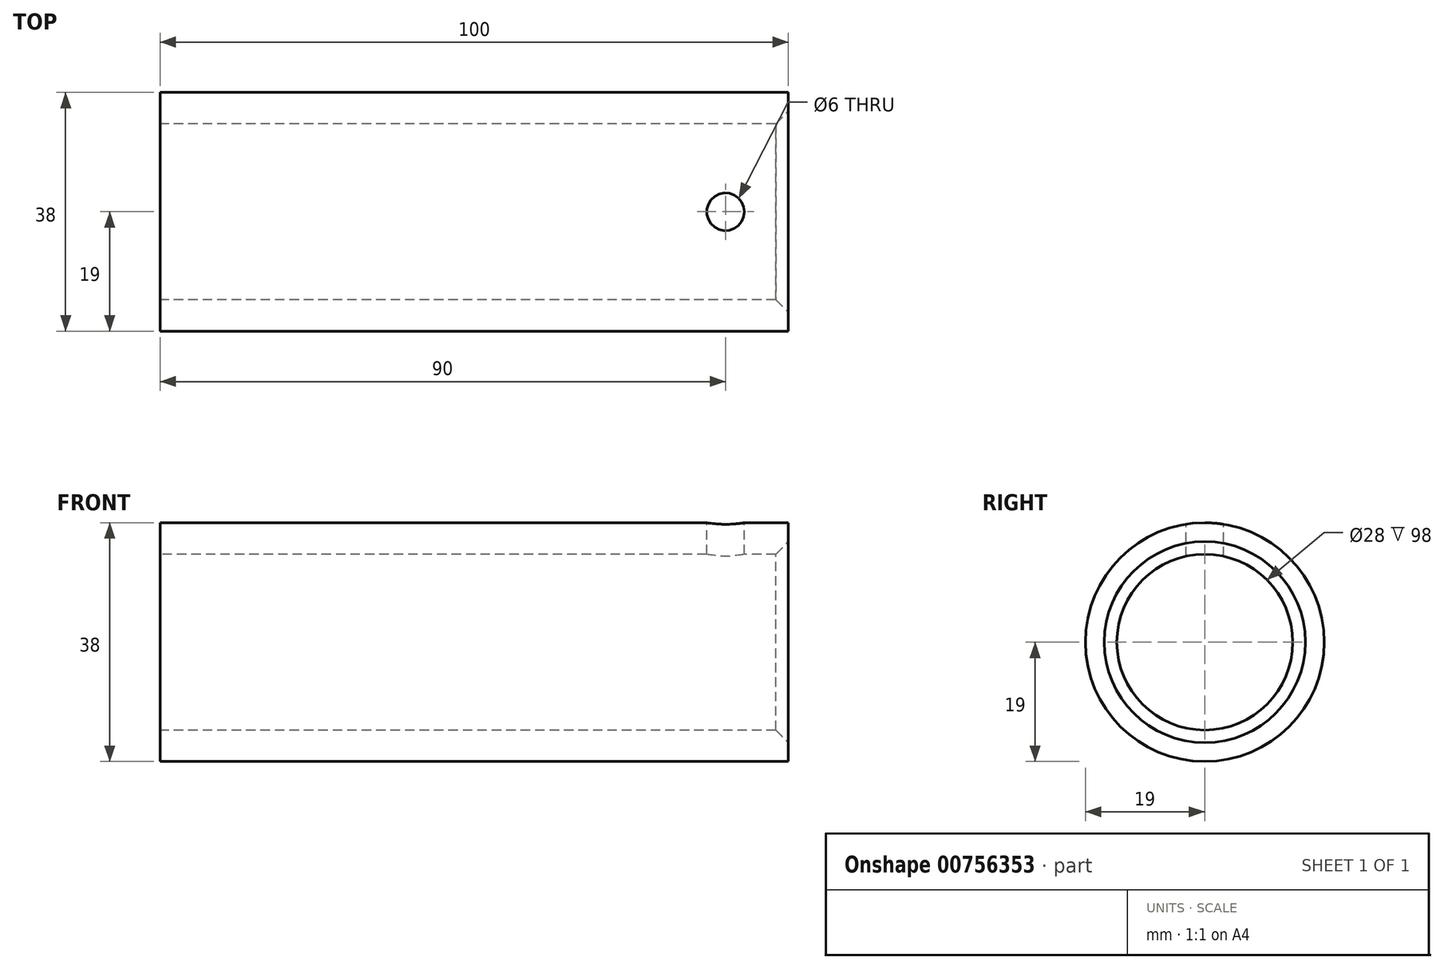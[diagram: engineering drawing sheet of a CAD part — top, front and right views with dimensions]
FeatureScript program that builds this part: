
annotation { "Feature Type Name" : "Feature", "Feature Type Description" : "" }
export const myFeature = defineFeature(function(context is Context, id is Id, definition is map)
    precondition{}
    {
        {
            var Q0;
            Q0=qCreatedBy(makeId("Right.planeOp"),FACE);
            var sketch = newSketch(context, id + "F0", { "sketchPlane" : qUnion([Q0])});
            skCircle(sketch, "E0", {"center": v(0, 0) * mm, "radius": 19 * mm});
            skCircle(sketch, "E1", {"center": v(0, 0) * mm, "radius": 14 * mm});
            skSolve(sketch);
        }
        {
            var Q0;
            Q0=makeQuery(id+"F0.imprint","IMPRINT",FACE,{"disambiguationData":[TD([[makeQuery(id+"F0.imprint","IMPRINT",EDGE,{"derivedFrom":sQuery(id+"F0.wireOp",EDGE,"E0")}),1.0]])]});
            extrude(context, id + "F1", {"entities" : qUnion([Q0]), "depth" : 100 * mm, "offsetDistance" : 25 * mm});
        }
        {
            var Q0;
            Q0=qCreatedBy(makeId("Top.planeOp"),FACE);
            cPlane(context, id + "F2", {"entities" : qUnion([Q0]), "cplaneType" : CPlaneType.OFFSET, "offset" : 19 * mm, "width" : 150 * mm, "height" : 150 * mm});
        }
        {
            var Q0;
            Q0=qCreatedBy(id+"F2.planeOp",FACE);
            var sketch = newSketch(context, id + "F3", { "sketchPlane" : qUnion([Q0])});
            skLineSegment(sketch, "E2", {"start": v(0, 0) * mm, "end": v(100, 0) * mm});
            skCircle(sketch, "E3", {"center": v(90, 0) * mm, "radius": 3 * mm});
            skSolve(sketch);
        }
        {
            var Q0;
            Q0=makeQuery(id+"F1.opExtrude","CAP_EDGE",EDGE,{"disambiguationData":[OSD([sQuery(id+"F0.wireOp",EDGE,"E1")])],"isStart":false});
            chamfer(context, id + "F4", {"entities" : qUnion([Q0]), "chamferType" : ChamferType.OFFSET_ANGLE, "width" : 2 * mm, "oppositeDirection" : false, "angle" : 45 * degree, "tangentPropagation" : true});
        }
        {
            var Q0;
            Q0=sQuery(id+"F3.wireOp",VERTEX,"E3.center");
            var Q1;
            Q1=makeQuery(id+"F1.opExtrude","SWEPT_BODY",BODY,{"disambiguationData":[OSD([sQuery(id+"F0.wireOp",EDGE,"E0"),sQuery(id+"F0.wireOp",EDGE,"E1")])]});
            hole(context, id + "F5", {"style" : HoleStyle.SIMPLE, "endStyle" : HoleEndStyle.BLIND, "holeDiameter" : 6 * mm, "majorDiameter" : 5 * mm, "holeDepth" : 15 * mm, "isTappedThrough" : true, "tappedDepth" : 12 * mm, "tapClearance" : 3, "locations" : qUnion([Q0]), "scope" : qUnion([Q1])});
        }
    });
